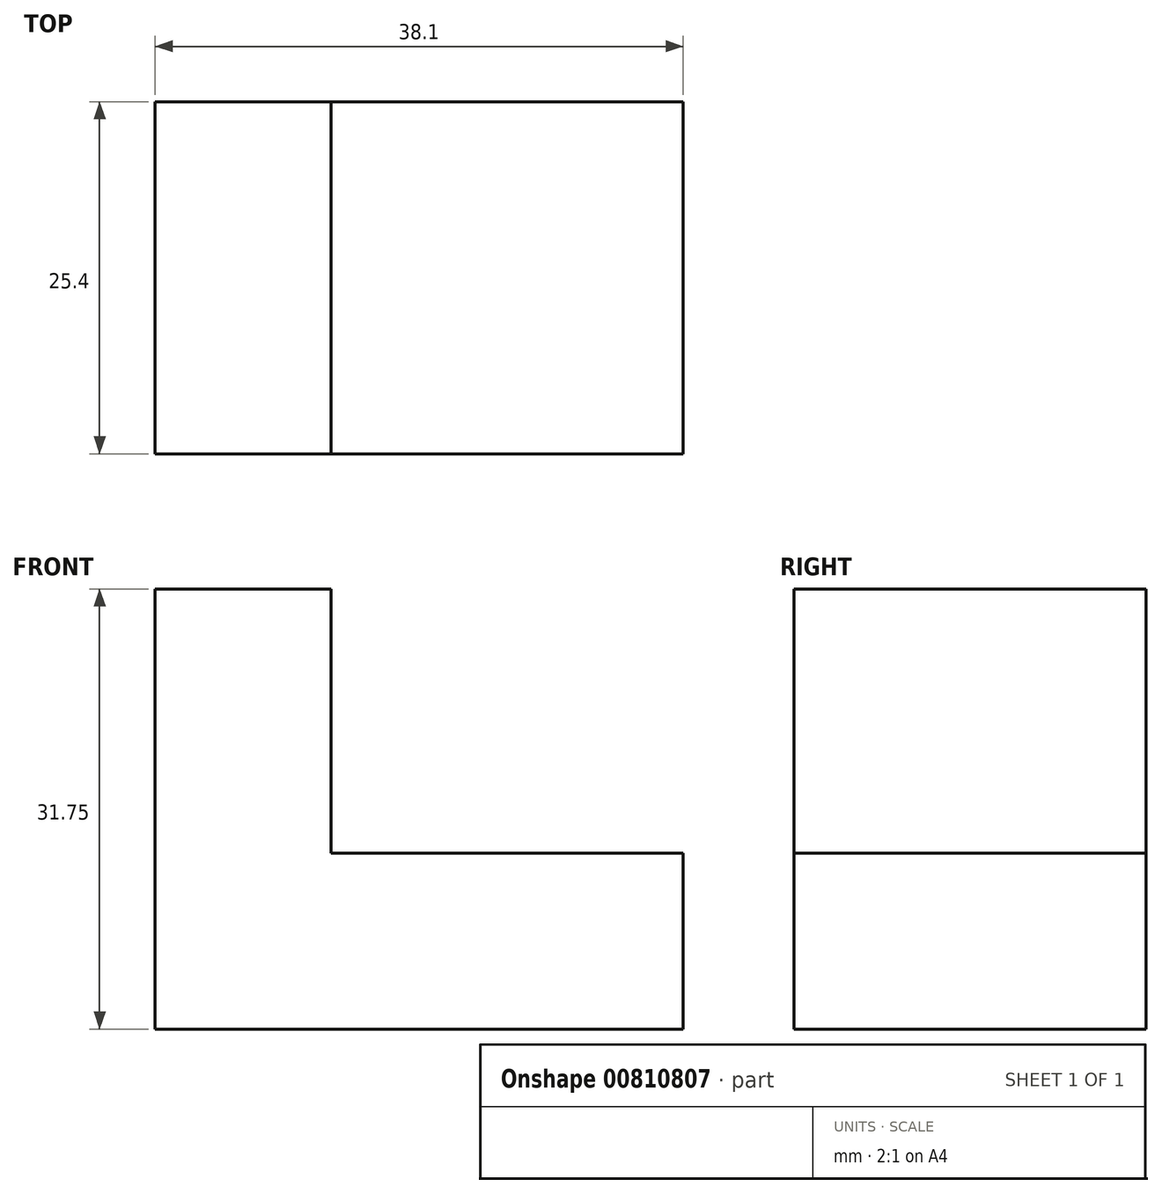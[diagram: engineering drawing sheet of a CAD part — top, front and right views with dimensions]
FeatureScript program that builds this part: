
annotation { "Feature Type Name" : "Feature", "Feature Type Description" : "" }
export const myFeature = defineFeature(function(context is Context, id is Id, definition is map)
    precondition{}
    {
        {
            var Q0;
            Q0=qCreatedBy(makeId("Front.planeOp"),FACE);
            var sketch = newSketch(context, id + "F0", { "sketchPlane" : qUnion([Q0])});
            skLineSegment(sketch, "E0", {"start": v(0, 0) * mm, "end": v(0, 31.75) * mm});
            skLineSegment(sketch, "E1", {"start": v(0, 0) * mm, "end": v(38.1, 0) * mm});
            skLineSegment(sketch, "E2", {"start": v(0, 31.75) * mm, "end": v(12.7, 31.75) * mm});
            skLineSegment(sketch, "E3", {"start": v(12.7, 31.75) * mm, "end": v(12.7, 12.7) * mm});
            skLineSegment(sketch, "E4", {"start": v(12.7, 12.7) * mm, "end": v(38.1, 12.7) * mm});
            skLineSegment(sketch, "E5", {"start": v(38.1, 12.7) * mm, "end": v(38.1, 0) * mm});
            skSolve(sketch);
        }
        {
            var Q0;
            Q0=makeQuery(id+"F0.imprint","IMPRINT",FACE,{"disambiguationData":[TD([[makeQuery(id+"F0.imprint","IMPRINT",EDGE,{"derivedFrom":sQuery(id+"F0.wireOp",EDGE,"E0")}),-1.0]])]});
            extrude(context, id + "F1", {"entities" : qUnion([Q0]), "depth" : 25.4 * mm, "offsetDistance" : 25.4 * mm});
        }
    });
